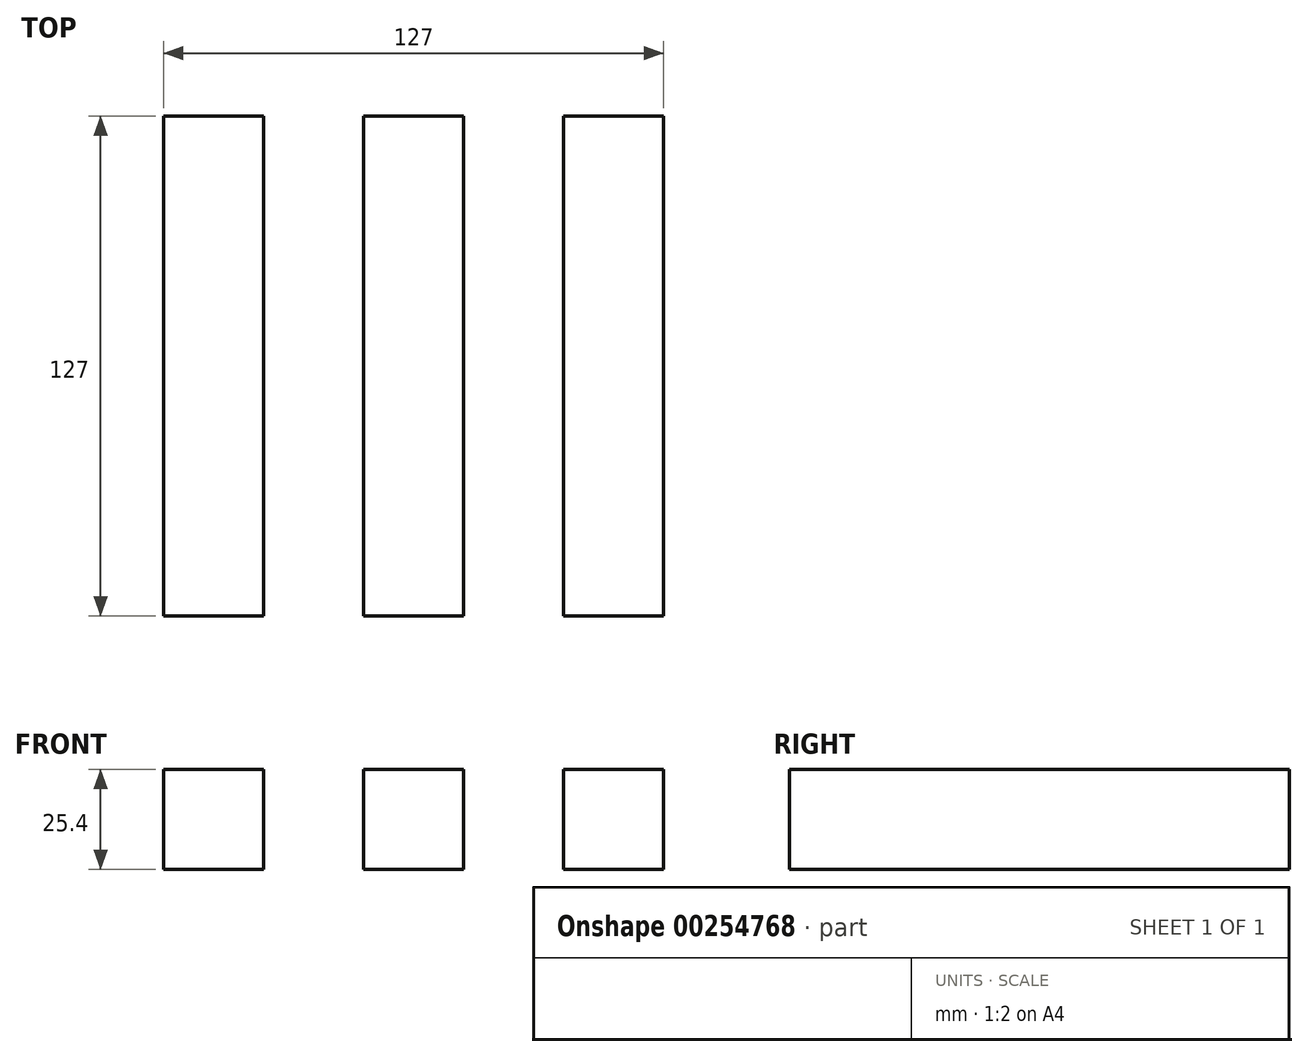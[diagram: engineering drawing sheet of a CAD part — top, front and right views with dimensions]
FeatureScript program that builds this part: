
annotation { "Feature Type Name" : "Feature", "Feature Type Description" : "" }
export const myFeature = defineFeature(function(context is Context, id is Id, definition is map)
    precondition{}
    {
        {
            var Q0;
            Q0=qCreatedBy(makeId("Front.planeOp"),FACE);
            var sketch = newSketch(context, id + "F0", { "sketchPlane" : qUnion([Q0])});
            skLineSegment(sketch, "E0.bottom", {"start": v(12.7, 12.7) * mm, "end": v(-12.7, 12.7) * mm});
            skLineSegment(sketch, "E0.top", {"start": v(12.7, -12.7) * mm, "end": v(-12.7, -12.7) * mm});
            skLineSegment(sketch, "E0.left", {"start": v(12.7, 12.7) * mm, "end": v(12.7, -12.7) * mm});
            skLineSegment(sketch, "E0.right", {"start": v(-12.7, 12.7) * mm, "end": v(-12.7, -12.7) * mm});
            skPoint(sketch, "E0.middle", {"position": v(0, 0) * mm});
            skLineSegment(sketch, "E1", {"start": v(0, 0) * mm, "end": v(50.8, 0) * mm});
            skLineSegment(sketch, "E2", {"start": v(0, 0) * mm, "end": v(-50.8, 0) * mm});
            skLineSegment(sketch, "E3.bottom", {"start": v(-38.1, 12.7) * mm, "end": v(-63.5, 12.7) * mm});
            skLineSegment(sketch, "E3.top", {"start": v(-38.1, -12.7) * mm, "end": v(-63.5, -12.7) * mm});
            skLineSegment(sketch, "E3.left", {"start": v(-38.1, 12.7) * mm, "end": v(-38.1, -12.7) * mm});
            skLineSegment(sketch, "E3.right", {"start": v(-63.5, 12.7) * mm, "end": v(-63.5, -12.7) * mm});
            skPoint(sketch, "E3.middle", {"position": v(-50.8, 0) * mm});
            skLineSegment(sketch, "E4.bottom", {"start": v(63.5, 12.7) * mm, "end": v(38.1, 12.7) * mm});
            skLineSegment(sketch, "E4.top", {"start": v(63.5, -12.7) * mm, "end": v(38.1, -12.7) * mm});
            skLineSegment(sketch, "E4.left", {"start": v(63.5, 12.7) * mm, "end": v(63.5, -12.7) * mm});
            skLineSegment(sketch, "E4.right", {"start": v(38.1, 12.7) * mm, "end": v(38.1, -12.7) * mm});
            skPoint(sketch, "E4.middle", {"position": v(50.8, 0) * mm});
            skSolve(sketch);
        }
        {
            var Q0;
            Q0 = qSketchRegion(id + "F0", true);
            extrude(context, id + "F1", {"entities" : qUnion([Q0]), "endBound" : BoundingType.SYMMETRIC, "depth" : 127 * mm});
        }
    });
